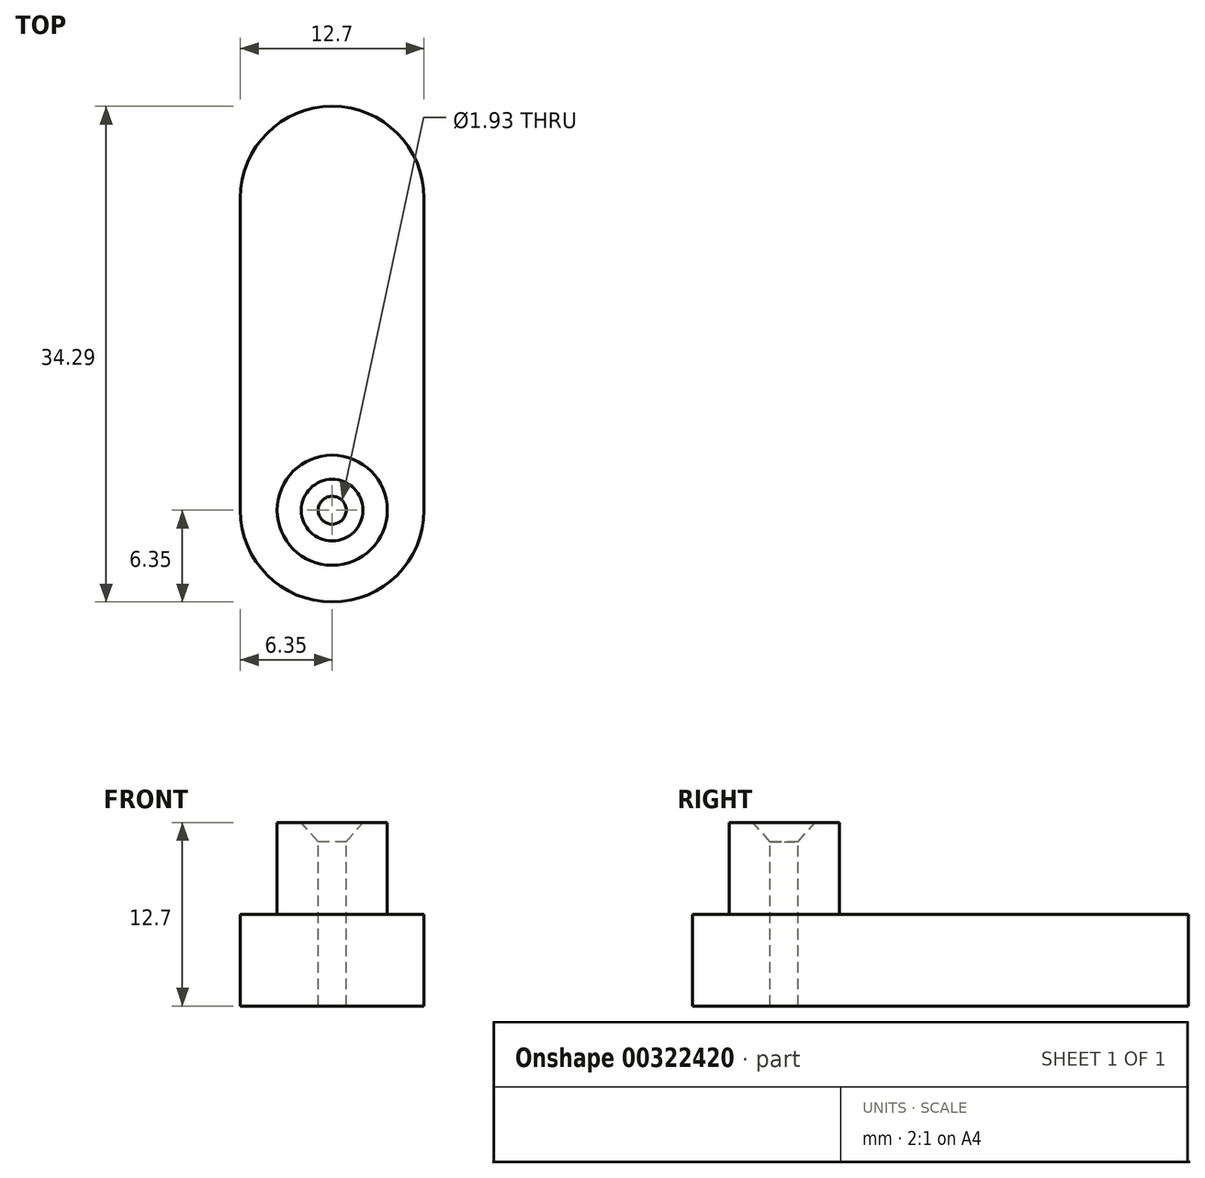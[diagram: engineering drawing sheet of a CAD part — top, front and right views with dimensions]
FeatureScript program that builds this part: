
annotation { "Feature Type Name" : "Feature", "Feature Type Description" : "" }
export const myFeature = defineFeature(function(context is Context, id is Id, definition is map)
    precondition{}
    {
        {
            var Q0;
            Q0=qCreatedBy(makeId("Top.planeOp"),FACE);
            var sketch = newSketch(context, id + "F0", { "sketchPlane" : qUnion([Q0])});
            skLineSegment(sketch, "E0", {"start": v(0, 0) * mm, "end": v(0, 12.7) * mm});
            skLineSegment(sketch, "E1", {"start": v(0, 12.7) * mm, "end": v(0, 34.3) * mm});
            skLineSegment(sketch, "E2", {"start": v(0, 34.29) * mm, "end": v(22.73, 67.98) * mm});
            skArc(sketch, "E3.0.startCap", {"start": v(6.35, 12.7) * mm, "mid": v(0, 6.35) * mm, "end": v(-6.35, 12.7) * mm});
            skArc(sketch, "E3.0.endCap", {"start": v(-6.35, 34.3) * mm, "mid": v(0, 40.64) * mm, "end": v(6.35, 34.3) * mm});
            skLineSegment(sketch, "E3.0.left", {"start": v(-6.35, 12.7) * mm, "end": v(-6.35, 34.3) * mm});
            skLineSegment(sketch, "E3.0.right", {"start": v(6.35, 12.7) * mm, "end": v(6.35, 34.3) * mm});
            skArc(sketch, "E3.1.startCap", {"start": v(6.35, 0) * mm, "mid": v(0, -6.35) * mm, "end": v(-6.35, 0) * mm});
            skArc(sketch, "E3.1.endCap", {"start": v(-6.35, 12.7) * mm, "mid": v(0, 19.05) * mm, "end": v(6.35, 12.7) * mm});
            skLineSegment(sketch, "E3.1.left", {"start": v(-6.35, 0) * mm, "end": v(-6.35, 12.7) * mm});
            skLineSegment(sketch, "E3.1.right", {"start": v(6.35, 0) * mm, "end": v(6.35, 12.7) * mm});
            skArc(sketch, "E3.2.startCap", {"start": v(5.26, 30.74) * mm, "mid": v(-3.55, 29.03) * mm, "end": v(-5.26, 37.84) * mm});
            skArc(sketch, "E3.2.endCap", {"start": v(17.46, 71.53) * mm, "mid": v(26.28, 73.25) * mm, "end": v(27.99, 64.43) * mm});
            skLineSegment(sketch, "E3.2.left", {"start": v(-5.26, 37.84) * mm, "end": v(17.46, 71.53) * mm});
            skLineSegment(sketch, "E3.2.right", {"start": v(5.26, 30.74) * mm, "end": v(27.99, 64.43) * mm});
            skSolve(sketch);
        }
        {
            var Q0;
            {var subQ5=sQuery(id+"F0.wireOp",EDGE,"E3.0.left");Q0=makeQuery(id+"F0.imprint","IMPRINT",FACE,{"disambiguationData":[TD([[makeQuery(id+"F0.imprint","IMPRINT",EDGE,{"derivedFrom":subQ5}),-1.0]])]});}
            var Q1;
            {var subQ0=sQuery(id+"F0.wireOp",EDGE,"E3.1.endCap");var subQ3=sQuery(id+"F0.wireOp",EDGE,"E1");var subQ4=makeQuery(id+"F0.imprint","INTERSECT",VERTEX,{"derivedFrom":[subQ3,subQ0]});Q1=makeQuery(id+"F0.imprint","IMPRINT",FACE,{"disambiguationData":[TD([[makeQuery(id+"F0.imprint","IMPRINT",EDGE,{"disambiguationData":[TD([[subQ4,-1.0]])],"derivedFrom":subQ3}),-1.0]])]});}
            var Q2;
            {var subQ3=sQuery(id+"F0.wireOp",EDGE,"E2");var subQ6=sQuery(id+"F0.wireOp",EDGE,"E1");var subQ8=makeQuery(id+"F0.imprint","INTERSECT",VERTEX,{"derivedFrom":[subQ6,subQ3]});Q2=makeQuery(id+"F0.imprint","IMPRINT",FACE,{"disambiguationData":[TD([[makeQuery(id+"F0.imprint","IMPRINT",EDGE,{"disambiguationData":[TD([[subQ8,1.0]])],"derivedFrom":subQ6}),1.0]])]});}
            var Q3;
            {var subQ7=sQuery(id+"F0.wireOp",EDGE,"E2");var subQ8=sQuery(id+"F0.wireOp",EDGE,"E1");var subQ9=makeQuery(id+"F0.imprint","INTERSECT",VERTEX,{"derivedFrom":[subQ8,subQ7]});Q3=makeQuery(id+"F0.imprint","IMPRINT",FACE,{"disambiguationData":[TD([[makeQuery(id+"F0.imprint","IMPRINT",EDGE,{"disambiguationData":[TD([[subQ9,1.0]])],"derivedFrom":subQ8}),-1.0]])]});}
            var Q4;
            {var subQ0=sQuery(id+"F0.wireOp",EDGE,"E3.2.endCap");Q4=makeQuery(id+"F0.imprint","IMPRINT",FACE,{"disambiguationData":[TD([[makeQuery(id+"F0.imprint","IMPRINT",EDGE,{"derivedFrom":subQ0}),-1.0]])]});}
            var Q5;
            {var subQ0=sQuery(id+"F0.wireOp",EDGE,"E1");var subQ1=sQuery(id+"F0.wireOp",EDGE,"E0");var subQ2=makeQuery(id+"F0.imprint","INTERSECT",VERTEX,{"derivedFrom":[subQ1,subQ0]});Q5=makeQuery(id+"F0.imprint","IMPRINT",FACE,{"disambiguationData":[TD([[makeQuery(id+"F0.imprint","IMPRINT",EDGE,{"disambiguationData":[TD([[subQ2,1.0]])],"derivedFrom":subQ1}),-1.0]])]});}
            var Q6;
            {var subQ0=sQuery(id+"F0.wireOp",EDGE,"E1");var subQ1=sQuery(id+"F0.wireOp",EDGE,"E0");var subQ2=makeQuery(id+"F0.imprint","INTERSECT",VERTEX,{"derivedFrom":[subQ1,subQ0]});Q6=makeQuery(id+"F0.imprint","IMPRINT",FACE,{"disambiguationData":[TD([[makeQuery(id+"F0.imprint","IMPRINT",EDGE,{"disambiguationData":[TD([[subQ2,1.0]])],"derivedFrom":subQ1}),1.0]])]});}
            var Q7;
            Q7=makeQuery(id+"F0.imprint","IMPRINT",FACE,{"disambiguationData":[TD([[makeQuery(id+"F0.imprint","IMPRINT",EDGE,{"derivedFrom":sQuery(id+"F0.wireOp",EDGE,"E3.1.startCap")}),-1.0]])]});
            extrude(context, id + "F1", {"entities" : qUnion([Q0, Q1, Q2, Q3, Q4, Q5, Q6, Q7]), "depth" : 6.35 * mm});
        }
        {
            var Q0;
            Q0=makeQuery(id+"F1.opExtrude","CAP_FACE",FACE,{"disambiguationData":[OSD([sQuery(id+"F0.wireOp",EDGE,"E3.0.left"),sQuery(id+"F0.wireOp",EDGE,"E3.0.right"),sQuery(id+"F0.wireOp",EDGE,"E3.1.startCap"),sQuery(id+"F0.wireOp",EDGE,"E3.1.left"),sQuery(id+"F0.wireOp",EDGE,"E3.1.right"),sQuery(id+"F0.wireOp",EDGE,"E3.2.startCap"),sQuery(id+"F0.wireOp",EDGE,"E3.2.endCap"),sQuery(id+"F0.wireOp",EDGE,"E3.2.left"),sQuery(id+"F0.wireOp",EDGE,"E3.2.right")])],"isStart":false});
            var sketch = newSketch(context, id + "F2", { "sketchPlane" : qUnion([Q0])});
            skLineSegment(sketch, "E4", {"start": v(0, 0) * mm, "end": v(0, 12.7) * mm, "construction": true});
            skLineSegment(sketch, "E5", {"start": v(0, 12.7) * mm, "end": v(0, 34.3) * mm, "construction": true});
            skLineSegment(sketch, "E6", {"start": v(0, 34.3) * mm, "end": v(22.73, 67.98) * mm, "construction": true});
            skCircle(sketch, "E7", {"center": v(0, 12.7) * mm, "radius": 3.81 * mm});
            skSolve(sketch);
        }
        {
            var Q0;
            Q0=makeQuery(id+"F2.imprint","IMPRINT",FACE,{"disambiguationData":[TD([[makeQuery(id+"F2.imprint","IMPRINT",EDGE,{"derivedFrom":sQuery(id+"F2.wireOp",EDGE,"E7")}),1.0]])]});
            extrude(context, id + "F3", {"entities" : qUnion([Q0]), "operationType" : NewBodyOperationType.ADD, "depth" : 6.35 * mm});
        }
        {
            var Q0;
            Q0=makeQuery(id+"F3.opExtrude","CAP_FACE",FACE,{"disambiguationData":[OSD([sQuery(id+"F2.wireOp",EDGE,"E7")])],"isStart":false});
            var sketch = newSketch(context, id + "F4", { "sketchPlane" : qUnion([Q0])});
            skPoint(sketch, "E8", {"position": v(0, 12.7) * mm});
            skSolve(sketch);
        }
        {
            var Q0;
            Q0=sQuery(id+"F4.wireOp",VERTEX,"E8");
            var Q1;
            Q1=makeQuery(id+"F1.opExtrude","SWEPT_BODY",BODY,{"disambiguationData":[OSD([sQuery(id+"F0.wireOp",EDGE,"E3.0.left"),sQuery(id+"F0.wireOp",EDGE,"E3.0.right"),sQuery(id+"F0.wireOp",EDGE,"E3.1.startCap"),sQuery(id+"F0.wireOp",EDGE,"E3.1.left"),sQuery(id+"F0.wireOp",EDGE,"E3.1.right"),sQuery(id+"F0.wireOp",EDGE,"E3.2.startCap"),sQuery(id+"F0.wireOp",EDGE,"E3.2.endCap"),sQuery(id+"F0.wireOp",EDGE,"E3.2.left"),sQuery(id+"F0.wireOp",EDGE,"E3.2.right")])]});
            hole(context, id + "F5", {"style" : HoleStyle.C_SINK, "endStyle" : HoleEndStyle.THROUGH, "standardTappedOrClearance" : lookupTablePath({ "standard" : "ANSI", "fit" : "Close", "size" : "#1", "type" : "Clearance" }), "standardBlindInLast" : lookupTablePath({ "fit" : "Close", "standard" : "ANSI", "size" : "#1", "type" : "Clearance" }), "holeDiameter" : 1.93 * mm, "cSinkDiameter" : 4.27 * mm, "cSinkAngle" : 82 * degree, "tappedDepth" : 12.7 * mm, "tapClearance" : 3, "locations" : qUnion([Q0]), "scope" : qUnion([Q1])});
        }
        {
            var Q0;
            Q0=makeQuery(id+"F1.opExtrude","CAP_FACE",FACE,{"disambiguationData":[OSD([sQuery(id+"F0.wireOp",EDGE,"E3.0.left"),sQuery(id+"F0.wireOp",EDGE,"E3.0.right"),sQuery(id+"F0.wireOp",EDGE,"E3.1.startCap"),sQuery(id+"F0.wireOp",EDGE,"E3.1.left"),sQuery(id+"F0.wireOp",EDGE,"E3.1.right"),sQuery(id+"F0.wireOp",EDGE,"E3.2.startCap"),sQuery(id+"F0.wireOp",EDGE,"E3.2.endCap"),sQuery(id+"F0.wireOp",EDGE,"E3.2.left"),sQuery(id+"F0.wireOp",EDGE,"E3.2.right")])],"isStart":false});
            var sketch = newSketch(context, id + "F6", { "sketchPlane" : qUnion([Q0])});
            skPoint(sketch, "E9", {"position": v(0, 0) * mm});
            skSolve(sketch);
        }
        {
            var Q0;
            Q0=sQuery(id+"F6.wireOp",VERTEX,"E9");
            var Q1;
            Q1=makeQuery(id+"F1.opExtrude","SWEPT_BODY",BODY,{"disambiguationData":[OSD([sQuery(id+"F0.wireOp",EDGE,"E3.0.left"),sQuery(id+"F0.wireOp",EDGE,"E3.0.right"),sQuery(id+"F0.wireOp",EDGE,"E3.1.startCap"),sQuery(id+"F0.wireOp",EDGE,"E3.1.left"),sQuery(id+"F0.wireOp",EDGE,"E3.1.right"),sQuery(id+"F0.wireOp",EDGE,"E3.2.startCap"),sQuery(id+"F0.wireOp",EDGE,"E3.2.endCap"),sQuery(id+"F0.wireOp",EDGE,"E3.2.left"),sQuery(id+"F0.wireOp",EDGE,"E3.2.right")])]});
            hole(context, id + "F7", {"style" : HoleStyle.SIMPLE, "endStyle" : HoleEndStyle.THROUGH, "holeDiameter" : 2.03 * mm, "tappedDepth" : 12.7 * mm, "tapClearance" : 3, "locations" : qUnion([Q0]), "scope" : qUnion([Q1])});
        }
    });
